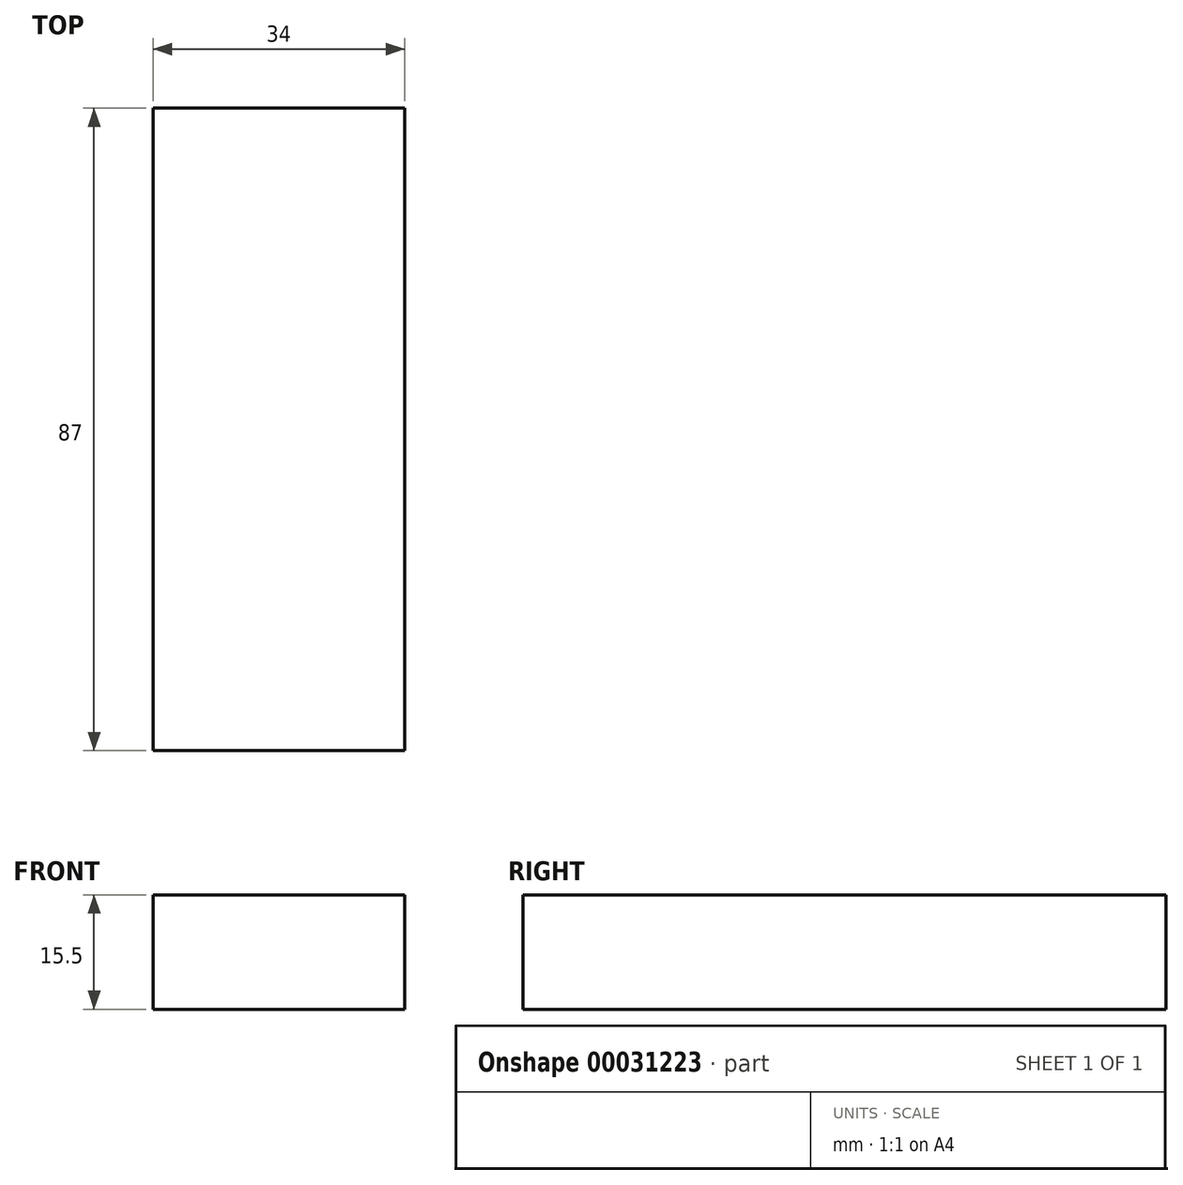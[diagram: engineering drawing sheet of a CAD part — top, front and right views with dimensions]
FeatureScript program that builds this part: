
annotation { "Feature Type Name" : "Feature", "Feature Type Description" : "" }
export const myFeature = defineFeature(function(context is Context, id is Id, definition is map)
    precondition{}
    {
        {
            var Q0;
            Q0=qCreatedBy(makeId("Top.planeOp"),FACE);
            var sketch = newSketch(context, id + "F0", { "sketchPlane" : qUnion([Q0])});
            skLineSegment(sketch, "E0.bottom", {"start": v(17, 43.5) * mm, "end": v(-17, 43.5) * mm});
            skLineSegment(sketch, "E0.top", {"start": v(17, -43.5) * mm, "end": v(-17, -43.5) * mm});
            skLineSegment(sketch, "E0.left", {"start": v(17, 43.5) * mm, "end": v(17, -43.5) * mm});
            skLineSegment(sketch, "E0.right", {"start": v(-17, 43.5) * mm, "end": v(-17, -43.5) * mm});
            skPoint(sketch, "E0.middle", {"position": v(0, 0) * mm});
            skSolve(sketch);
        }
        {
            var Q0;
            Q0 = qSketchRegion(id + "F0", true);
            extrude(context, id + "F1", {"entities" : qUnion([Q0]), "depth" : 15.5 * mm});
        }
    });
